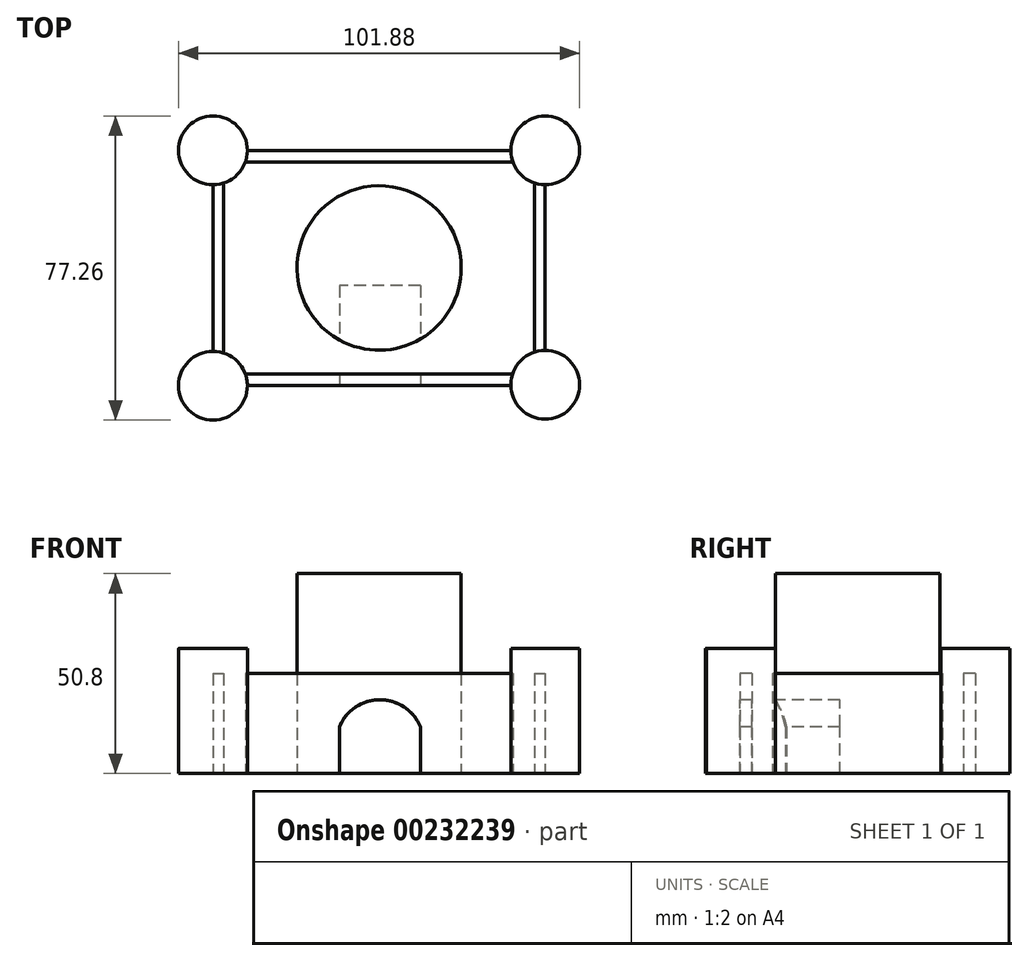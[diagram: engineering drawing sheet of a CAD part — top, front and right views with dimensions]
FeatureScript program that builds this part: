
annotation { "Feature Type Name" : "Feature", "Feature Type Description" : "" }
export const myFeature = defineFeature(function(context is Context, id is Id, definition is map)
    precondition{}
    {
        {
            var Q0;
            Q0=qCreatedBy(makeId("Top.planeOp"),FACE);
            var sketch = newSketch(context, id + "F0", { "sketchPlane" : qUnion([Q0])});
            skLineSegment(sketch, "E0.bottom", {"start": v(33.46, 29.88) * mm, "end": v(-33.46, 29.88) * mm});
            skLineSegment(sketch, "E0.top", {"start": v(33.46, -29.88) * mm, "end": v(-33.45, -29.88) * mm});
            skLineSegment(sketch, "E0.left", {"start": v(42.2, 21.14) * mm, "end": v(42.2, -20.93) * mm});
            skLineSegment(sketch, "E0.right", {"start": v(-42.2, 21.14) * mm, "end": v(-42.2, -21.16) * mm});
            skPoint(sketch, "E0.middle", {"position": v(0, 0) * mm});
            skCircle(sketch, "E1", {"center": v(0, 0) * mm, "radius": 20.88 * mm});
            skCircle(sketch, "E2", {"center": v(-42.2, 29.88) * mm, "radius": 8.74 * mm});
            skCircle(sketch, "E3", {"center": v(42.2, 29.88) * mm, "radius": 8.74 * mm});
            skCircle(sketch, "E4", {"center": v(42.2, -29.67) * mm, "radius": 8.74 * mm});
            skCircle(sketch, "E5", {"center": v(-42.19, -29.9) * mm, "radius": 8.74 * mm});
            skLineSegment(sketch, "E6.trimOffspring", {"start": v(42.2, -29.67) * mm, "end": v(42.2, -29.88) * mm});
            skPoint(sketch, "E7.orphan", {"position": v(-42.2, -29.88) * mm});
            skLineSegment(sketch, "E8.bottom", {"start": v(33.9, -26.9) * mm, "end": v(-33.97, -26.9) * mm});
            skLineSegment(sketch, "E8.top", {"start": v(33.98, 26.9) * mm, "end": v(-33.98, 26.9) * mm});
            skLineSegment(sketch, "E8.left", {"start": v(39.47, -21.37) * mm, "end": v(39.47, 21.58) * mm});
            skLineSegment(sketch, "E8.right", {"start": v(-39.47, -21.6) * mm, "end": v(-39.47, 21.58) * mm});
            skPoint(sketch, "E9.orphan", {"position": v(-39.47, 26.9) * mm});
            skPoint(sketch, "E10.orphan", {"position": v(39.47, 26.9) * mm});
            skPoint(sketch, "E11.orphan", {"position": v(-39.47, -26.9) * mm});
            skPoint(sketch, "E12.orphan", {"position": v(39.47, -26.9) * mm});
            skSolve(sketch);
        }
        {
            var Q0;
            {var subQ0=sQuery(id+"F0.wireOp",EDGE,"E0.bottom");Q0=makeQuery(id+"F0.imprint","IMPRINT",FACE,{"disambiguationData":[TD([[makeQuery(id+"F0.imprint","IMPRINT",EDGE,{"derivedFrom":subQ0}),1.0]])]});}
            var Q1;
            {var subQ0=sQuery(id+"F0.wireOp",EDGE,"E0.right");Q1=makeQuery(id+"F0.imprint","IMPRINT",FACE,{"disambiguationData":[TD([[makeQuery(id+"F0.imprint","IMPRINT",EDGE,{"derivedFrom":subQ0}),1.0]])]});}
            var Q2;
            {var subQ0=sQuery(id+"F0.wireOp",EDGE,"E0.left");Q2=makeQuery(id+"F0.imprint","IMPRINT",FACE,{"disambiguationData":[TD([[makeQuery(id+"F0.imprint","IMPRINT",EDGE,{"derivedFrom":subQ0}),-1.0]])]});}
            var Q3;
            {var subQ0=sQuery(id+"F0.wireOp",EDGE,"E0.top");Q3=makeQuery(id+"F0.imprint","IMPRINT",FACE,{"disambiguationData":[TD([[makeQuery(id+"F0.imprint","IMPRINT",EDGE,{"derivedFrom":subQ0}),-1.0]])]});}
            extrude(context, id + "F1", {"entities" : qUnion([Q0, Q1, Q2, Q3]), "depth" : 25.4 * mm});
        }
        {
            var Q0;
            {var subQ0=sQuery(id+"F0.wireOp",EDGE,"E2");var subQ1=makeQuery(id+"F0.imprint","INTERSECT",VERTEX,{"derivedFrom":[sQuery(id+"F0.wireOp",EDGE,"E0.bottom"),subQ0]});Q0=makeQuery(id+"F0.imprint","IMPRINT",FACE,{"disambiguationData":[TD([[makeQuery(id+"F0.imprint","IMPRINT",EDGE,{"disambiguationData":[TD([[subQ1,-1.0]])],"derivedFrom":subQ0}),1.0]])]});}
            var Q1;
            {var subQ0=sQuery(id+"F0.wireOp",EDGE,"E3");var subQ1=makeQuery(id+"F0.imprint","INTERSECT",VERTEX,{"derivedFrom":[sQuery(id+"F0.wireOp",EDGE,"E0.bottom"),subQ0]});Q1=makeQuery(id+"F0.imprint","IMPRINT",FACE,{"disambiguationData":[TD([[makeQuery(id+"F0.imprint","IMPRINT",EDGE,{"disambiguationData":[TD([[subQ1,-1.0]])],"derivedFrom":subQ0}),1.0]])]});}
            var Q2;
            {var subQ0=sQuery(id+"F0.wireOp",EDGE,"E4");var subQ1=makeQuery(id+"F0.imprint","INTERSECT",VERTEX,{"derivedFrom":[sQuery(id+"F0.wireOp",EDGE,"E0.left"),subQ0]});Q2=makeQuery(id+"F0.imprint","IMPRINT",FACE,{"disambiguationData":[TD([[makeQuery(id+"F0.imprint","IMPRINT",EDGE,{"disambiguationData":[TD([[subQ1,-1.0]])],"derivedFrom":subQ0}),1.0]])]});}
            var Q3;
            {var subQ0=sQuery(id+"F0.wireOp",EDGE,"E5");var subQ1=makeQuery(id+"F0.imprint","INTERSECT",VERTEX,{"derivedFrom":[sQuery(id+"F0.wireOp",EDGE,"E0.top"),subQ0]});Q3=makeQuery(id+"F0.imprint","IMPRINT",FACE,{"disambiguationData":[TD([[makeQuery(id+"F0.imprint","IMPRINT",EDGE,{"disambiguationData":[TD([[subQ1,-1.0]])],"derivedFrom":subQ0}),1.0]])]});}
            extrude(context, id + "F2", {"entities" : qUnion([Q0, Q1, Q2, Q3]), "depth" : 31.75 * mm});
        }
        {
            var Q0;
            Q0=makeQuery(id+"F0.imprint","IMPRINT",FACE,{"disambiguationData":[TD([[makeQuery(id+"F0.imprint","IMPRINT",EDGE,{"derivedFrom":sQuery(id+"F0.wireOp",EDGE,"E1")}),1.0]])]});
            extrude(context, id + "F3", {"entities" : qUnion([Q0]), "depth" : 50.8 * mm});
        }
        {
            var Q0;
            Q0=makeQuery(id+"F1.opExtrude","SWEPT_FACE",FACE,{"disambiguationData":[OSD([sQuery(id+"F0.wireOp",EDGE,"E0.top")])]});
            var sketch = newSketch(context, id + "F4", { "sketchPlane" : qUnion([Q0])});
            skLineSegment(sketch, "E13.bottom", {"start": v(-10.07, 0) * mm, "end": v(10.5, 0) * mm});
            skLineSegment(sketch, "E13.left", {"start": v(-10.07, 0) * mm, "end": v(-10.07, 11.89) * mm});
            skLineSegment(sketch, "E13.right", {"start": v(10.5, 0) * mm, "end": v(10.5, 11.89) * mm});
            skArc(sketch, "E14", {"start": v(10.5, 11.89) * mm, "mid": v(0.21, 18.74) * mm, "end": v(-10.07, 11.89) * mm});
            skSolve(sketch);
        }
        {
            var Q0;
            Q0=makeQuery(id+"F4.imprint","IMPRINT",FACE,{"disambiguationData":[TD([[makeQuery(id+"F4.imprint","IMPRINT",EDGE,{"derivedFrom":sQuery(id+"F4.wireOp",EDGE,"E13.bottom")}),-1.0]])]});
            extrude(context, id + "F5", {"entities" : qUnion([Q0]), "operationType" : NewBodyOperationType.REMOVE, "oppositeDirection" : true, "depth" : 25.4 * mm});
        }
    });
